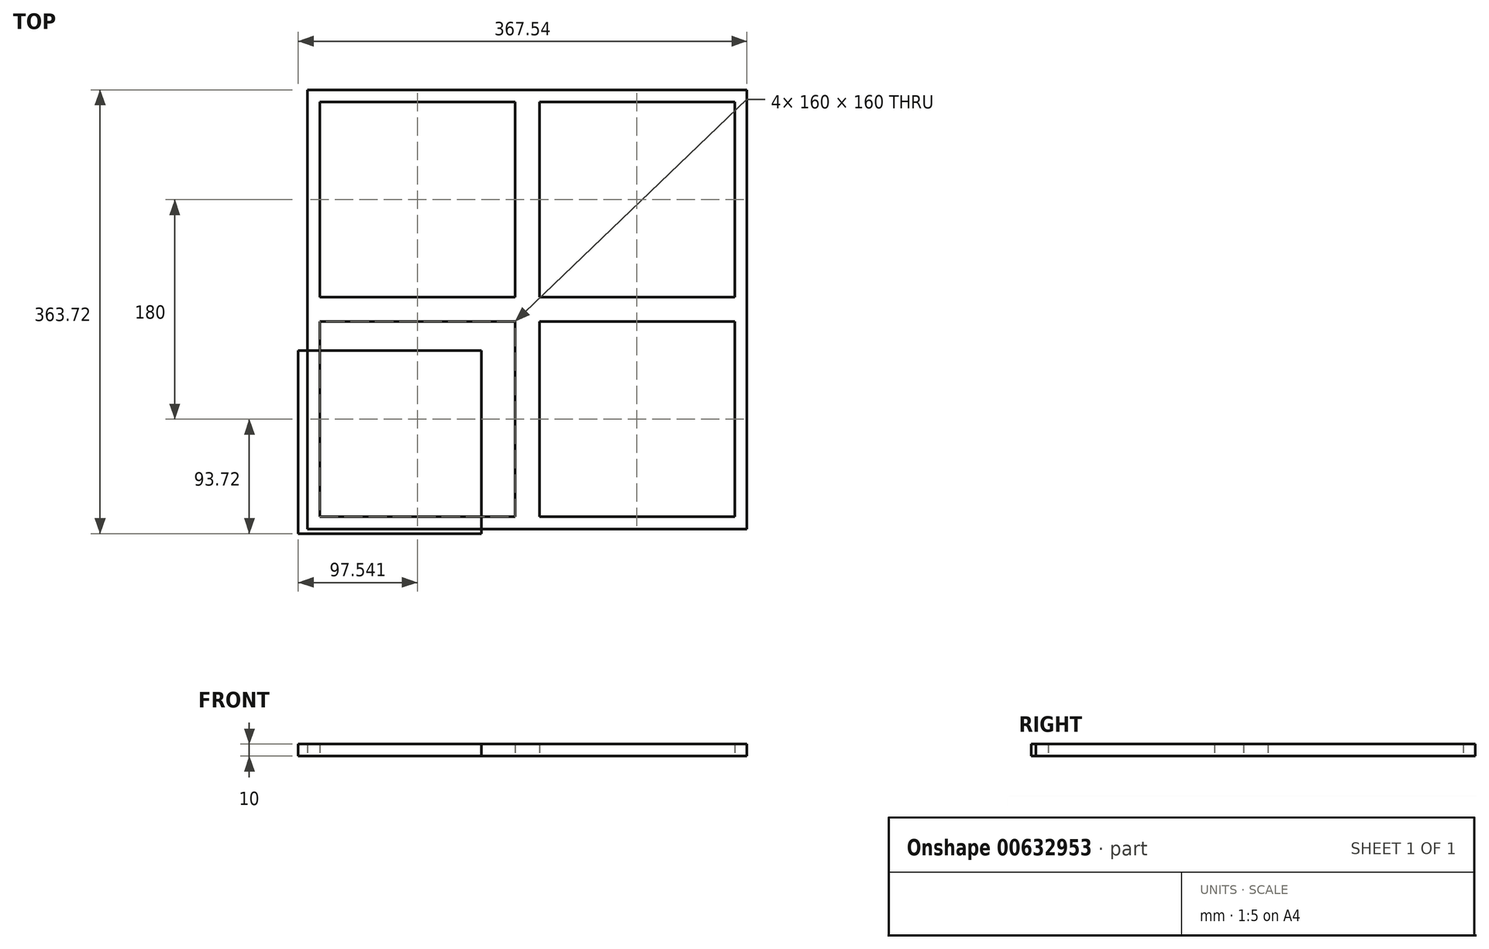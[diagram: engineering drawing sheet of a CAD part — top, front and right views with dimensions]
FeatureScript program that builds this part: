
annotation { "Feature Type Name" : "Feature", "Feature Type Description" : "" }
export const myFeature = defineFeature(function(context is Context, id is Id, definition is map)
    precondition{}
    {
        {
            var Q0;
            Q0=qCreatedBy(makeId("Top.planeOp"),FACE);
            var sketch = newSketch(context, id + "F0", { "sketchPlane" : qUnion([Q0])});
            skLineSegment(sketch, "E0.top", {"start": v(-75, -75) * mm, "end": v(75, -75) * mm});
            skLineSegment(sketch, "E0.left", {"start": v(-75, 75) * mm, "end": v(-75, -75) * mm});
            skLineSegment(sketch, "E0.right", {"start": v(75, 75) * mm, "end": v(75, -75) * mm});
            skLineSegment(sketch, "E1", {"start": v(-75, 75) * mm, "end": v(75, 75) * mm});
            skSolve(sketch);
        }
        {
            var Q0;
            Q0 = qSketchRegion(id + "F0", true);
            extrude(context, id + "F1", {"entities" : qUnion([Q0]), "depth" : 10 * mm, "offsetDistance" : 25 * mm});
        }
        {
            var Q0;
            Q0=qCreatedBy(makeId("Top.planeOp"),FACE);
            var sketch = newSketch(context, id + "F2", { "sketchPlane" : qUnion([Q0])});
            skLineSegment(sketch, "E2.bottom", {"start": v(-67.46, 288.72) * mm, "end": v(292.54, 288.72) * mm});
            skLineSegment(sketch, "E2.top", {"start": v(-67.46, -71.28) * mm, "end": v(292.54, -71.28) * mm});
            skLineSegment(sketch, "E2.left", {"start": v(-67.46, 288.72) * mm, "end": v(-67.46, -71.28) * mm});
            skLineSegment(sketch, "E2.right", {"start": v(292.54, 288.72) * mm, "end": v(292.54, -71.28) * mm});
            skLineSegment(sketch, "E3.bottom", {"start": v(-57.46, 278.72) * mm, "end": v(102.54, 278.72) * mm});
            skLineSegment(sketch, "E3.top", {"start": v(-57.46, 118.72) * mm, "end": v(102.54, 118.72) * mm});
            skLineSegment(sketch, "E3.left", {"start": v(-57.46, 278.72) * mm, "end": v(-57.46, 118.72) * mm});
            skLineSegment(sketch, "E3.right", {"start": v(102.54, 278.72) * mm, "end": v(102.54, 118.72) * mm});
            skLineSegment(sketch, "E4.bottom", {"start": v(122.54, 278.72) * mm, "end": v(282.54, 278.72) * mm});
            skLineSegment(sketch, "E4.top", {"start": v(122.54, 118.72) * mm, "end": v(282.54, 118.72) * mm});
            skLineSegment(sketch, "E4.left", {"start": v(122.54, 278.72) * mm, "end": v(122.54, 118.72) * mm});
            skLineSegment(sketch, "E4.right", {"start": v(282.54, 278.72) * mm, "end": v(282.54, 118.72) * mm});
            skLineSegment(sketch, "E5.bottom", {"start": v(122.54, 98.72) * mm, "end": v(282.54, 98.72) * mm});
            skLineSegment(sketch, "E5.top", {"start": v(122.54, -61.28) * mm, "end": v(282.54, -61.28) * mm});
            skLineSegment(sketch, "E5.left", {"start": v(122.54, 98.72) * mm, "end": v(122.54, -61.28) * mm});
            skLineSegment(sketch, "E5.right", {"start": v(282.54, 98.72) * mm, "end": v(282.54, -61.28) * mm});
            skLineSegment(sketch, "E6.bottom", {"start": v(-57.46, 98.72) * mm, "end": v(102.54, 98.72) * mm});
            skLineSegment(sketch, "E6.top", {"start": v(-57.46, -61.28) * mm, "end": v(102.54, -61.28) * mm});
            skLineSegment(sketch, "E6.left", {"start": v(-57.46, 98.72) * mm, "end": v(-57.46, -61.28) * mm});
            skLineSegment(sketch, "E6.right", {"start": v(102.54, 98.72) * mm, "end": v(102.54, -61.28) * mm});
            skSolve(sketch);
        }
        {
            var Q0;
            Q0 = qSketchRegion(id + "F2", true);
            extrude(context, id + "F3", {"entities" : qUnion([Q0]), "depth" : 10 * mm, "offsetDistance" : 25 * mm});
        }
    });
